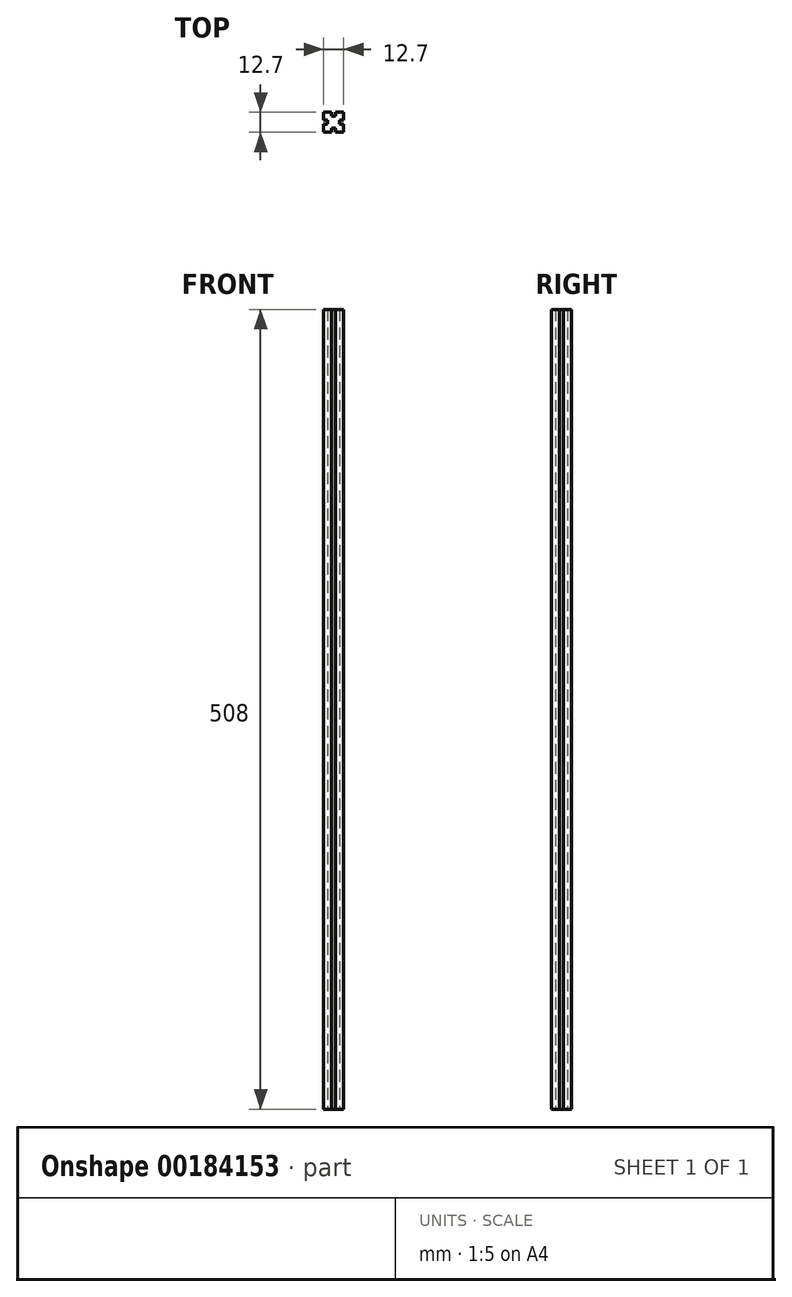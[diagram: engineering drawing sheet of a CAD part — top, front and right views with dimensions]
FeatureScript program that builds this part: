
annotation { "Feature Type Name" : "Feature", "Feature Type Description" : "" }
export const myFeature = defineFeature(function(context is Context, id is Id, definition is map)
    precondition{}
    {
        {
            var Q0;
            Q0=qCreatedBy(makeId("Top.planeOp"),FACE);
            var sketch = newSketch(context, id + "F0", { "sketchPlane" : qUnion([Q0])});
            skLineSegment(sketch, "E0.bottom", {"start": v(-6.35, 6.35) * mm, "end": v(6.35, 6.35) * mm});
            skLineSegment(sketch, "E0.top", {"start": v(-6.35, -6.35) * mm, "end": v(6.35, -6.35) * mm});
            skLineSegment(sketch, "E0.left", {"start": v(-6.35, 6.35) * mm, "end": v(-6.35, -6.35) * mm});
            skLineSegment(sketch, "E0.right", {"start": v(6.35, 6.35) * mm, "end": v(6.35, -6.35) * mm});
            skPoint(sketch, "E0.middle", {"position": v(0, 0) * mm});
            skLineSegment(sketch, "E1.bottom", {"start": v(-1.27, -6.35) * mm, "end": v(1.27, -6.35) * mm});
            skLineSegment(sketch, "E1.top", {"start": v(-1.27, -3.8) * mm, "end": v(1.27, -3.8) * mm});
            skLineSegment(sketch, "E1.left", {"start": v(-1.27, -6.35) * mm, "end": v(-1.27, -3.8) * mm});
            skLineSegment(sketch, "E1.right", {"start": v(1.27, -6.35) * mm, "end": v(1.27, -3.8) * mm});
            skLineSegment(sketch, "E2.1.0", {"start": v(6.35, -1.27) * mm, "end": v(3.8, -1.27) * mm});
            skLineSegment(sketch, "E2.1.1", {"start": v(3.8, -1.27) * mm, "end": v(3.8, 1.27) * mm});
            skLineSegment(sketch, "E2.1.2", {"start": v(6.35, 1.27) * mm, "end": v(3.8, 1.27) * mm});
            skLineSegment(sketch, "E2.2.0", {"start": v(1.27, 6.35) * mm, "end": v(1.27, 3.8) * mm});
            skLineSegment(sketch, "E2.2.1", {"start": v(1.27, 3.8) * mm, "end": v(-1.27, 3.8) * mm});
            skLineSegment(sketch, "E2.2.2", {"start": v(-1.27, 6.35) * mm, "end": v(-1.27, 3.8) * mm});
            skLineSegment(sketch, "E2.3.0", {"start": v(-6.35, 1.27) * mm, "end": v(-3.8, 1.27) * mm});
            skLineSegment(sketch, "E2.3.1", {"start": v(-3.8, 1.27) * mm, "end": v(-3.8, -1.27) * mm});
            skLineSegment(sketch, "E2.3.2", {"start": v(-6.35, -1.27) * mm, "end": v(-3.8, -1.27) * mm});
            skSolve(sketch);
        }
        {
            var Q0;
            Q0=makeQuery(id+"F0.imprint","IMPRINT",FACE,{"disambiguationData":[TD([[makeQuery(id+"F0.imprint","IMPRINT",EDGE,{"derivedFrom":sQuery(id+"F0.wireOp",EDGE,"E1.top")}),1.0]])]});
            extrude(context, id + "F1", {"entities" : qUnion([Q0]), "depth" : 508 * mm});
        }
    });
